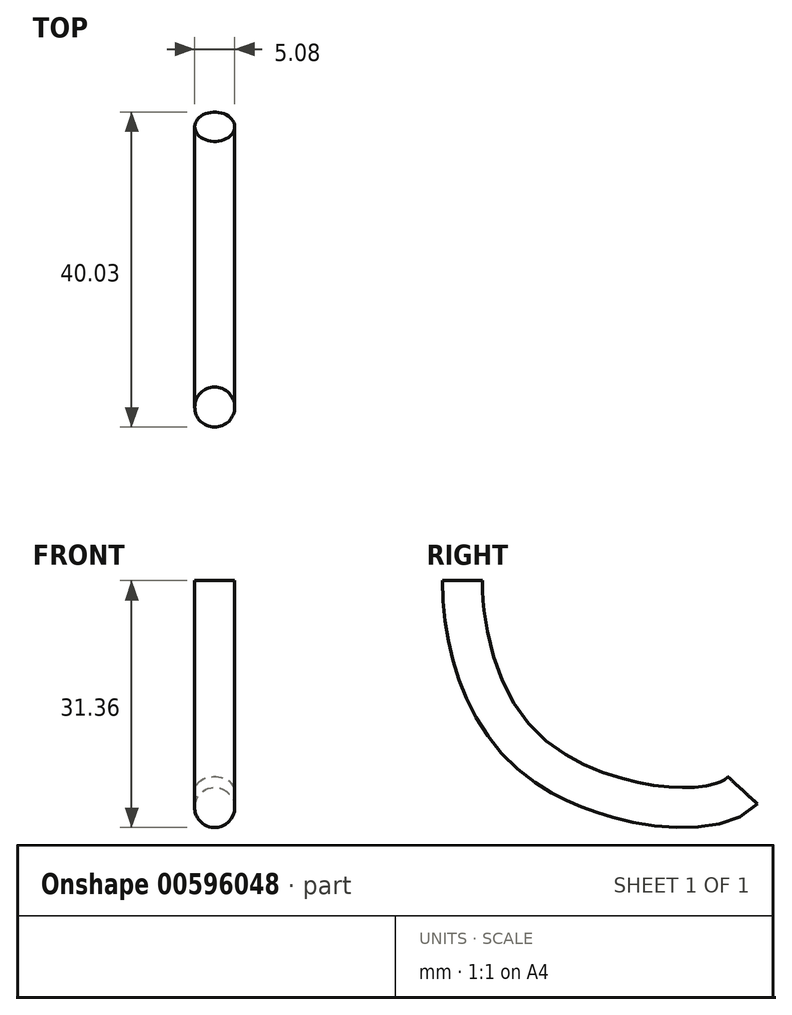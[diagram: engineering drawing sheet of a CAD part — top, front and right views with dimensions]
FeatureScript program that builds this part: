
annotation { "Feature Type Name" : "Feature", "Feature Type Description" : "" }
export const myFeature = defineFeature(function(context is Context, id is Id, definition is map)
    precondition{}
    {
        {
            var Q0;
            Q0=qCreatedBy(makeId("Top.planeOp"),FACE);
            var sketch = newSketch(context, id + "F0", { "sketchPlane" : qUnion([Q0])});
            skCircle(sketch, "E0", {"center": v(0, 0) * mm, "radius": 2.54 * mm});
            skSolve(sketch);
        }
        {
            var Q0;
            Q0=qCreatedBy(makeId("Right.planeOp"),FACE);
            var sketch = newSketch(context, id + "F1", { "sketchPlane" : qUnion([Q0])});
            skFitSpline(sketch, "E1", {"points": [v(0, 0) * mm, v(8.88, -22.2) * mm, v(35.62, -26.67) * mm], "startDerivative": vector(0, -31.76) * mm, "endDerivative": vector(21.76, 23.55) * mm});
            skSolve(sketch);
        }
        {
            var Q0;
            Q0 = qSketchRegion(id + "F0", true);
            var Q1;
            Q1 = qConstructionFilter(qBodyType(qCreatedBy(id + "F1" ,EDGE), BodyType.WIRE), ConstructionObject.NO);
            sweep(context, id + "F2", {"profiles" : qUnion([Q0]), "path" : qUnion([Q1])});
        }
    });
